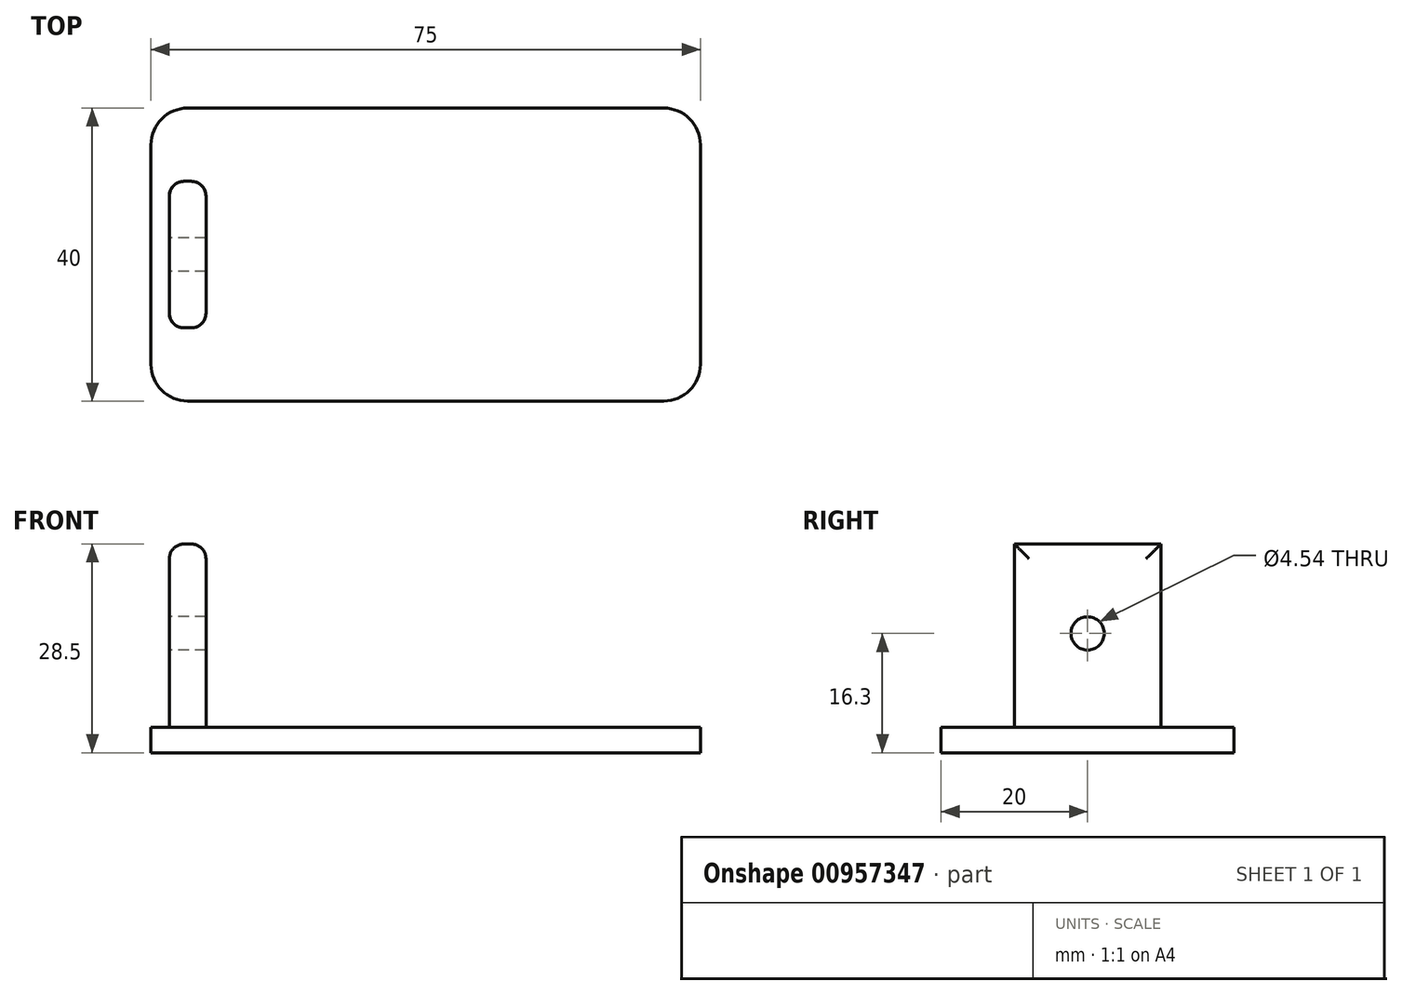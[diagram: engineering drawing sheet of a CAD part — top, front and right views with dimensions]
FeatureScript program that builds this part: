
annotation { "Feature Type Name" : "Feature", "Feature Type Description" : "" }
export const myFeature = defineFeature(function(context is Context, id is Id, definition is map)
    precondition{}
    {
        {
            var Q0;
            Q0=qCreatedBy(makeId("Top.planeOp"),FACE);
            var sketch = newSketch(context, id + "F0", { "sketchPlane" : qUnion([Q0])});
            skLineSegment(sketch, "E0.bottom", {"start": v(-50, 19.13) * mm, "end": v(15, 19.13) * mm});
            skLineSegment(sketch, "E0.top", {"start": v(-50, -20.87) * mm, "end": v(15, -20.87) * mm});
            skLineSegment(sketch, "E0.left", {"start": v(-55, 14.13) * mm, "end": v(-55, -15.87) * mm});
            skLineSegment(sketch, "E0.right", {"start": v(20, 14.13) * mm, "end": v(20, -15.87) * mm});
            skLineSegment(sketch, "E1", {"start": v(-55, -0.87) * mm, "end": v(20, -0.87) * mm, "construction": true});
            skLineSegment(sketch, "E2.bottom", {"start": v(-55, 9.13) * mm, "end": v(-45, 9.13) * mm});
            skLineSegment(sketch, "E2.top", {"start": v(-55, -10.87) * mm, "end": v(-45, -10.87) * mm});
            skLineSegment(sketch, "E2.left", {"start": v(-55, 9.13) * mm, "end": v(-55, -10.87) * mm});
            skLineSegment(sketch, "E2.right", {"start": v(-45, 9.13) * mm, "end": v(-45, -10.87) * mm});
            skPoint(sketch, "E3.visualSharp", {"position": v(20, 19.13) * mm});
            skArc(sketch, "E3.filletArc", {"start": v(20, 14.13) * mm, "mid": v(18.54, 17.67) * mm, "end": v(15, 19.13) * mm});
            skPoint(sketch, "E4.visualSharp", {"position": v(20, -20.87) * mm});
            skArc(sketch, "E4.filletArc", {"start": v(15, -20.87) * mm, "mid": v(18.54, -19.4) * mm, "end": v(20, -15.87) * mm});
            skPoint(sketch, "E5.visualSharp", {"position": v(-55, -20.87) * mm});
            skArc(sketch, "E5.filletArc", {"start": v(-55, -15.87) * mm, "mid": v(-53.54, -19.4) * mm, "end": v(-50, -20.87) * mm});
            skPoint(sketch, "E6.visualSharp", {"position": v(-55, 19.13) * mm});
            skArc(sketch, "E6.filletArc", {"start": v(-50, 19.13) * mm, "mid": v(-53.54, 17.67) * mm, "end": v(-55, 14.13) * mm});
            skLineSegment(sketch, "E7", {"start": v(-52.5, 9.13) * mm, "end": v(-52.5, -10.87) * mm});
            skLineSegment(sketch, "E8", {"start": v(-47.5, 9.13) * mm, "end": v(-47.5, -10.87) * mm});
            skSolve(sketch);
        }
        {
            var Q0;
            Q0=makeQuery(id+"F0.imprint","IMPRINT",FACE,{"disambiguationData":[TD([[makeQuery(id+"F0.imprint","IMPRINT",EDGE,{"derivedFrom":sQuery(id+"F0.wireOp",EDGE,"E0.bottom")}),-1.0]])]});
            var Q1;
            {var subQ5=sQuery(id+"F0.wireOp",EDGE,"E7");Q1=makeQuery(id+"F0.imprint","IMPRINT",FACE,{"disambiguationData":[TD([[makeQuery(id+"F0.imprint","IMPRINT",EDGE,{"derivedFrom":subQ5}),-1.0]])]});}
            var Q2;
            {var subQ0=sQuery(id+"F0.wireOp",EDGE,"E2.right");Q2=makeQuery(id+"F0.imprint","IMPRINT",FACE,{"disambiguationData":[TD([[makeQuery(id+"F0.imprint","IMPRINT",EDGE,{"derivedFrom":subQ0}),-1.0]])]});}
            extrude(context, id + "F1", {"entities" : qUnion([Q0, Q1, Q2]), "depth" : 3.5 * mm, "offsetDistance" : 25 * mm});
        }
        {
            var Q0;
            {var subQ0=sQuery(id+"F0.wireOp",EDGE,"E7");Q0=makeQuery(id+"F0.imprint","IMPRINT",FACE,{"disambiguationData":[TD([[makeQuery(id+"F0.imprint","IMPRINT",EDGE,{"derivedFrom":subQ0}),1.0]])]});}
            extrude(context, id + "F2", {"entities" : qUnion([Q0]), "operationType" : NewBodyOperationType.ADD, "depth" : 28.5 * mm, "offsetDistance" : 25 * mm});
        }
        {
            var Q0;
            Q0=makeQuery(id+"F2.opExtrude","SWEPT_FACE",FACE,{"disambiguationData":[OSD([sQuery(id+"F0.wireOp",EDGE,"E7")])]});
            var sketch = newSketch(context, id + "F3", { "sketchPlane" : qUnion([Q0])});
            skCircle(sketch, "E9", {"center": v(0.87, 16.3) * mm, "radius": 2.27 * mm});
            skSolve(sketch);
        }
        {
            var Q0;
            Q0=makeQuery(id+"F3.imprint","IMPRINT",FACE,{"disambiguationData":[TD([[makeQuery(id+"F3.imprint","IMPRINT",EDGE,{"derivedFrom":sQuery(id+"F3.wireOp",EDGE,"E9")}),1.0]])]});
            extrude(context, id + "F4", {"entities" : qUnion([Q0]), "operationType" : NewBodyOperationType.REMOVE, "oppositeDirection" : true, "depth" : 5 * mm, "offsetDistance" : 25 * mm});
        }
        {
            var Q0;
            Q0=makeQuery(id+"F2.opExtrude","CAP_EDGE",EDGE,{"disambiguationData":[OSD([sQuery(id+"F0.wireOp",EDGE,"E7")])],"isStart":false});
            var Q1;
            Q1=makeQuery(id+"F2.opExtrude","CAP_EDGE",EDGE,{"disambiguationData":[OSD([sQuery(id+"F0.wireOp",EDGE,"E8")])],"isStart":false});
            var Q2;
            Q2=makeQuery(id+"F2.opExtrude","SWEPT_EDGE",EDGE,{"disambiguationData":[OSD([sQuery(id+"F0.wireOp",EDGE,"E2.top"),sQuery(id+"F0.wireOp",EDGE,"E8")])]});
            var Q3;
            Q3=makeQuery(id+"F2.opExtrude","SWEPT_EDGE",EDGE,{"disambiguationData":[OSD([sQuery(id+"F0.wireOp",EDGE,"E2.top"),sQuery(id+"F0.wireOp",EDGE,"E7")])]});
            var Q4;
            Q4=makeQuery(id+"F2.opExtrude","SWEPT_EDGE",EDGE,{"disambiguationData":[OSD([sQuery(id+"F0.wireOp",EDGE,"E2.bottom"),sQuery(id+"F0.wireOp",EDGE,"E7")])]});
            var Q5;
            Q5=makeQuery(id+"F2.opExtrude","SWEPT_EDGE",EDGE,{"disambiguationData":[OSD([sQuery(id+"F0.wireOp",EDGE,"E2.bottom"),sQuery(id+"F0.wireOp",EDGE,"E8")])]});
            fillet(context, id + "F5", {"entities" : qUnion([Q0, Q1, Q2, Q3, Q4, Q5]), "radius" : 2 * mm, "tangentPropagation" : true, "allowEdgeOverflow" : false});
        }
    });
